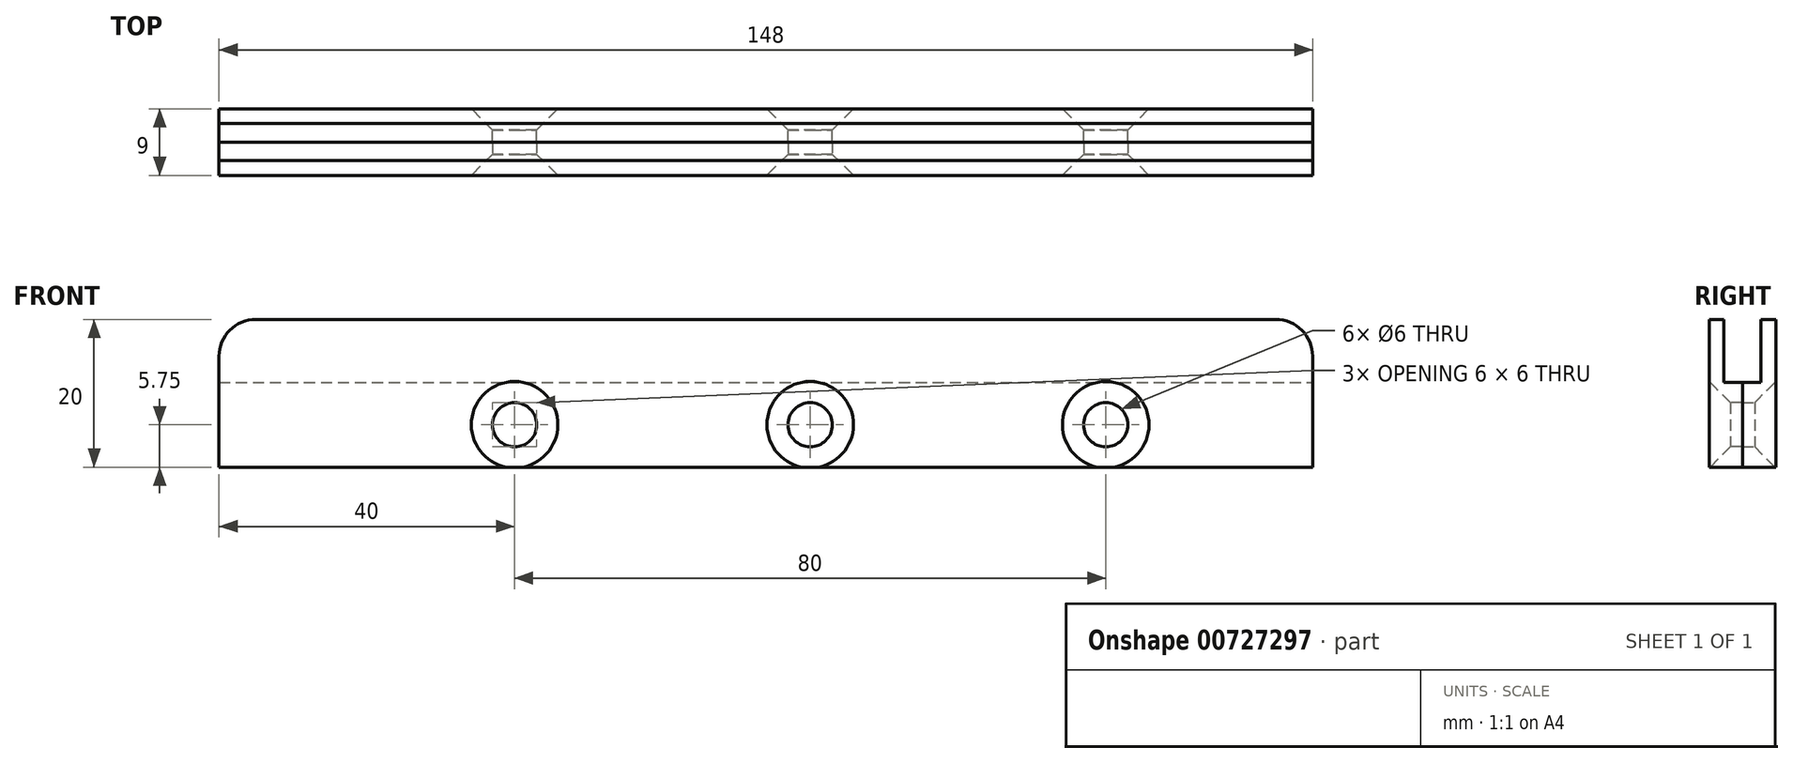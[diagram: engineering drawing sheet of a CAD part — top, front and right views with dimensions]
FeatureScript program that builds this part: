
annotation { "Feature Type Name" : "Feature", "Feature Type Description" : "" }
export const myFeature = defineFeature(function(context is Context, id is Id, definition is map)
    precondition{}
    {
        {
            var Q0;
            Q0=qCreatedBy(makeId("Front.planeOp"),FACE);
            var sketch = newSketch(context, id + "F0", { "sketchPlane" : qUnion([Q0])});
            skLineSegment(sketch, "E0.bottom", {"start": v(-74, 0) * mm, "end": v(74, 0) * mm});
            skLineSegment(sketch, "E0.top", {"start": v(-74, 11.5) * mm, "end": v(74, 11.5) * mm});
            skLineSegment(sketch, "E0.left", {"start": v(-74, 0) * mm, "end": v(-74, 11.5) * mm});
            skLineSegment(sketch, "E0.right", {"start": v(74, 0) * mm, "end": v(74, 11.5) * mm});
            skPoint(sketch, "E1", {"position": v(46, 5.75) * mm});
            skPoint(sketch, "E2.1.0.0", {"position": v(6, 5.75) * mm});
            skPoint(sketch, "E2.2.0.0", {"position": v(-34, 5.75) * mm});
            skLineSegment(sketch, "E2.direction1", {"start": v(46, 5.75) * mm, "end": v(6, 5.75) * mm, "construction": true});
            skSolve(sketch);
        }
        {
            var Q0;
            Q0=qSketchRegion(id+"F0",true);
            extrude(context, id + "F1", {"entities" : qUnion([Q0]), "oppositeDirection" : true, "depth" : 2.5 * mm, "offsetDistance" : 25 * mm});
        }
        {
            var Q0;
            Q0=makeQuery(id+"F1.opExtrude","CAP_FACE",FACE,{"disambiguationData":[OSD([sQuery(id+"F0.wireOp",EDGE,"E0.bottom"),sQuery(id+"F0.wireOp",EDGE,"E0.top"),sQuery(id+"F0.wireOp",EDGE,"E0.left"),sQuery(id+"F0.wireOp",EDGE,"E0.right")])],"isStart":false});
            var sketch = newSketch(context, id + "F2", { "sketchPlane" : qUnion([Q0])});
            skLineSegment(sketch, "E3.bottom", {"start": v(-74, 0) * mm, "end": v(74, 0) * mm});
            skLineSegment(sketch, "E3.top", {"start": v(-74, 20) * mm, "end": v(74, 20) * mm});
            skLineSegment(sketch, "E3.left", {"start": v(-74, 0) * mm, "end": v(-74, 20) * mm});
            skLineSegment(sketch, "E3.right", {"start": v(74, 0) * mm, "end": v(74, 20) * mm});
            skSolve(sketch);
        }
        {
            var Q0;
            Q0=qSketchRegion(id+"F2",true);
            extrude(context, id + "F3", {"entities" : qUnion([Q0]), "operationType" : NewBodyOperationType.ADD, "depth" : 2 * mm, "offsetDistance" : 25 * mm});
        }
        {
            var Q0;
            Q0=makeQuery(id+"F3.opExtrude","CAP_FACE",FACE,{"disambiguationData":[OSD([sQuery(id+"F2.wireOp",EDGE,"E3.bottom"),sQuery(id+"F2.wireOp",EDGE,"E3.top"),sQuery(id+"F2.wireOp",EDGE,"E3.left"),sQuery(id+"F2.wireOp",EDGE,"E3.right")])],"isStart":false});
            var sketch = newSketch(context, id + "F4", { "sketchPlane" : qUnion([Q0])});
            skPoint(sketch, "E4.0", {"position": v(-46, 5.75) * mm});
            skPoint(sketch, "E4.1", {"position": v(-6, 5.75) * mm});
            skPoint(sketch, "E4.2", {"position": v(34, 5.75) * mm});
            skSolve(sketch);
        }
        {
            var Q0;
            Q0=sQuery(id+"F4.wireOp",VERTEX,"E4.0");
            var Q1;
            Q1=sQuery(id+"F4.wireOp",VERTEX,"E4.1");
            var Q2;
            Q2=sQuery(id+"F4.wireOp",VERTEX,"E4.2");
            var Q3;
            Q3=makeQuery(id+"F1.opExtrude","SWEPT_BODY",BODY,{"disambiguationData":[OSD([sQuery(id+"F0.wireOp",EDGE,"E0.bottom"),sQuery(id+"F0.wireOp",EDGE,"E0.top"),sQuery(id+"F0.wireOp",EDGE,"E0.left"),sQuery(id+"F0.wireOp",EDGE,"E0.right")])]});
            hole(context, id + "F5", {"style" : HoleStyle.C_SINK, "endStyle" : HoleEndStyle.THROUGH, "holeDiameter" : 6 * mm, "cSinkDiameter" : 11.7 * mm, "cSinkAngle" : 90 * degree, "majorDiameter" : 5 * mm, "isTappedThrough" : true, "tappedDepth" : 12 * mm, "tapClearance" : 3, "locations" : qUnion([Q0, Q1, Q2]), "scope" : qUnion([Q3])});
        }
        {
            var Q0;
            Q0=makeQuery(id+"F3.opExtrude","SWEPT_EDGE",EDGE,{"disambiguationData":[OSD([sQuery(id+"F2.wireOp",EDGE,"E3.top"),sQuery(id+"F2.wireOp",EDGE,"E3.right")])]});
            var Q1;
            Q1=makeQuery(id+"F3.opExtrude","SWEPT_EDGE",EDGE,{"disambiguationData":[OSD([sQuery(id+"F2.wireOp",EDGE,"E3.top"),sQuery(id+"F2.wireOp",EDGE,"E3.left")])]});
            fillet(context, id + "F6", {"entities" : qUnion([Q0, Q1]), "radius" : 5 * mm, "tangentPropagation" : true, "allowEdgeOverflow" : false});
        }
        {
            var Q0;
            Q0=makeQuery(id+"F1.opExtrude","SWEPT_BODY",BODY,{"disambiguationData":[OSD([sQuery(id+"F0.wireOp",EDGE,"E0.bottom"),sQuery(id+"F0.wireOp",EDGE,"E0.top"),sQuery(id+"F0.wireOp",EDGE,"E0.left"),sQuery(id+"F0.wireOp",EDGE,"E0.right")])]});
            var Q1;
            Q1=qCreatedBy(makeId("Front.planeOp"),FACE);
            mirror(context, id + "F7", {"entities" : qUnion([Q0]), "mirrorPlane" : qUnion([Q1])});
        }
    });
